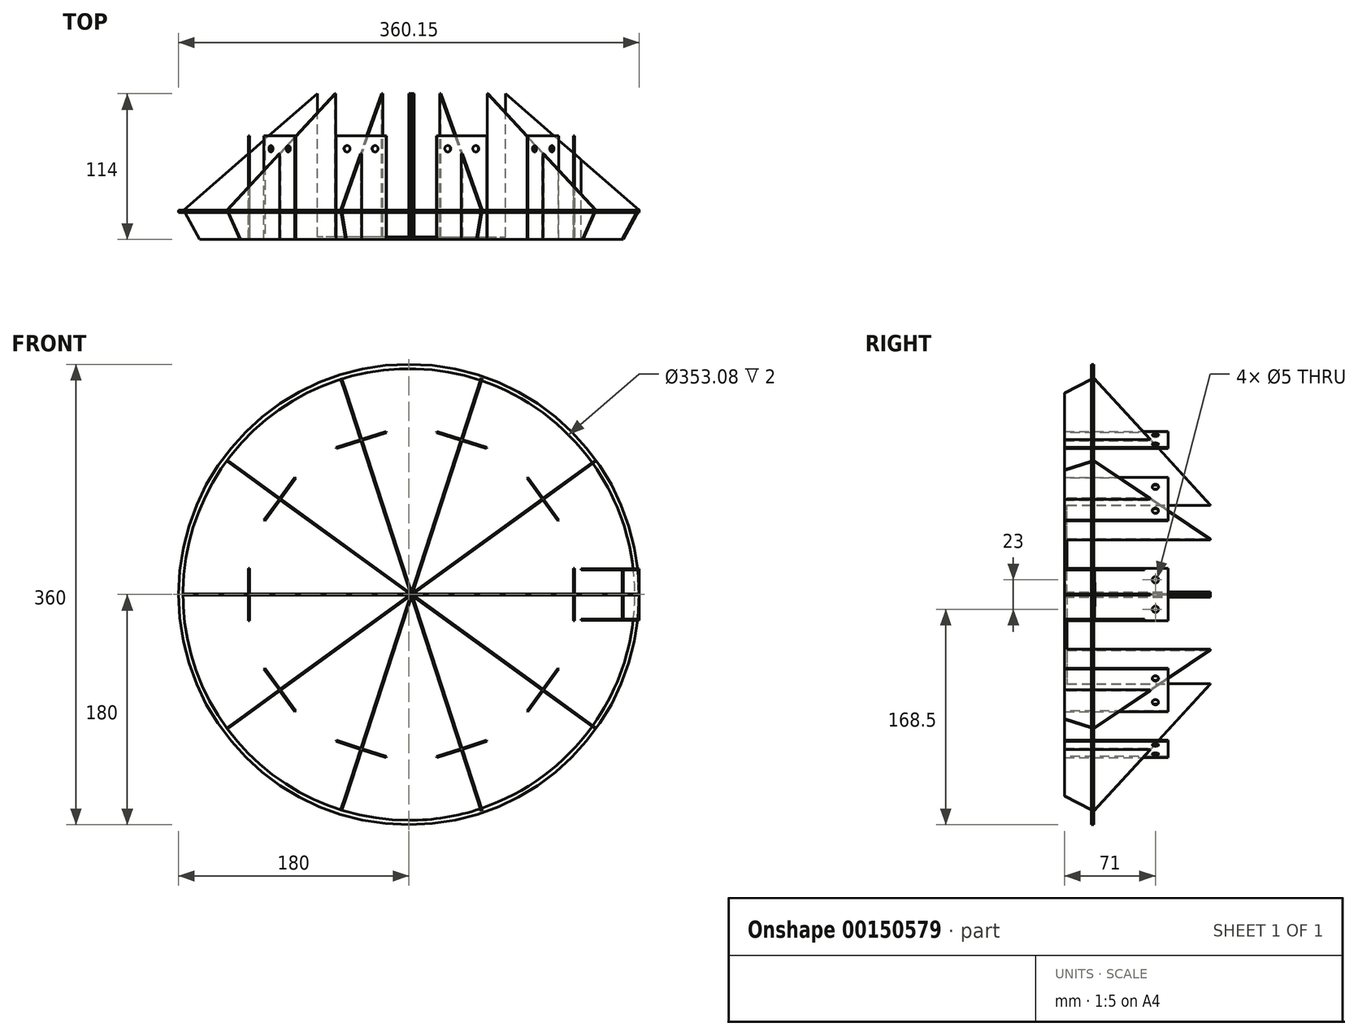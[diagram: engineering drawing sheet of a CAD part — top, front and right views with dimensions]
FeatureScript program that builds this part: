
annotation { "Feature Type Name" : "Feature", "Feature Type Description" : "" }
export const myFeature = defineFeature(function(context is Context, id is Id, definition is map)
    precondition{}
    {
        {
            var Q0;
            Q0=qCreatedBy(makeId("Top.planeOp"),FACE);
            var sketch = newSketch(context, id + "F0", { "sketchPlane" : qUnion([Q0])});
            skLineSegment(sketch, "E0", {"start": v(75.5, 0) * mm, "end": v(180, 0) * mm});
            skLineSegment(sketch, "E1", {"start": v(0, 0) * mm, "end": v(0, -23) * mm, "construction": true});
            skLineSegment(sketch, "E2", {"start": v(75.5, -23) * mm, "end": v(167.5, -23) * mm});
            skLineSegment(sketch, "E3", {"start": v(167.5, -23) * mm, "end": v(180, 0) * mm});
            skLineSegment(sketch, "E4", {"start": v(0, 91) * mm, "end": v(75.5, 91) * mm, "construction": true});
            skLineSegment(sketch, "E5", {"start": v(134.64, 39.5) * mm, "end": v(180, 0) * mm});
            skLineSegment(sketch, "E6", {"start": v(75.5, 39.5) * mm, "end": v(75.5, 0) * mm});
            skLineSegment(sketch, "E7", {"start": v(75.5, 0) * mm, "end": v(75.5, -23) * mm});
            skLineSegment(sketch, "E8", {"start": v(75.5, 0) * mm, "end": v(0, 0) * mm, "construction": true});
            skLineSegment(sketch, "E9", {"start": v(0, -23) * mm, "end": v(75.5, -23) * mm});
            skLineSegment(sketch, "E10", {"start": v(0, -23) * mm, "end": v(0, -21) * mm});
            skLineSegment(sketch, "E11", {"start": v(0, -21) * mm, "end": v(75.5, -21) * mm});
            skLineSegment(sketch, "E12", {"start": v(0, -21) * mm, "end": v(0, 91) * mm});
            skLineSegment(sketch, "E13", {"start": v(0, 91) * mm, "end": v(2, 91) * mm});
            skLineSegment(sketch, "E14", {"start": v(2, 91) * mm, "end": v(2, -21) * mm});
            skLineSegment(sketch, "E15", {"start": v(167.5, -23) * mm, "end": v(230.94, -23) * mm, "construction": true});
            skLineSegment(sketch, "E16", {"start": v(230.94, -23) * mm, "end": v(230.94, 39.5) * mm, "construction": true});
            skLineSegment(sketch, "E17", {"start": v(230.94, 39.5) * mm, "end": v(19.42, 39.5) * mm, "construction": true});
            skLineSegment(sketch, "E18", {"start": v(134.64, 39.5) * mm, "end": v(75.5, 39.5) * mm});
            skLineSegment(sketch, "E19", {"start": v(75.5, 39.5) * mm, "end": v(75.5, 91) * mm});
            skLineSegment(sketch, "E20", {"start": v(75.5, 91) * mm, "end": v(134.64, 39.5) * mm});
            skSolve(sketch);
        }
        {
            var Q0;
            Q0 = qSketchRegion(id + "F0", true);
            extrude(context, id + "F1", {"entities" : qUnion([Q0]), "endBound" : BoundingType.SYMMETRIC, "depth" : 1 * mm});
        }
        {
            var Q0;
            Q0=qCreatedBy(makeId("Top.planeOp"),FACE);
            var sketch = newSketch(context, id + "F2", { "sketchPlane" : qUnion([Q0])});
            skLineSegment(sketch, "E21.bottom", {"start": v(15, 5.01) * mm, "end": v(21.3, 5.01) * mm});
            skLineSegment(sketch, "E21.top", {"start": v(15, 0) * mm, "end": v(21.3, 0) * mm});
            skLineSegment(sketch, "E21.left", {"start": v(15, 5.01) * mm, "end": v(15, 0) * mm});
            skLineSegment(sketch, "E21.right", {"start": v(21.3, 5.01) * mm, "end": v(21.3, 0) * mm});
            skSolve(sketch);
        }
        {
            var Q0;
            Q0 = qSketchRegion(id + "F2", true);
            extrude(context, id + "F3", {"entities" : qUnion([Q0]), "operationType" : NewBodyOperationType.ADD, "endBound" : BoundingType.SYMMETRIC, "depth" : 38.5 * mm});
        }
        {
            var Q0;
            Q0=makeQuery(id+"F3.opExtrude","CAP_FACE",FACE,{"disambiguationData":[OSD([sQuery(id+"F2.wireOp",EDGE,"E21.bottom"),sQuery(id+"F2.wireOp",EDGE,"E21.top"),sQuery(id+"F2.wireOp",EDGE,"E21.left"),sQuery(id+"F2.wireOp",EDGE,"E21.right")])],"isStart":false});
            var sketch = newSketch(context, id + "F4", { "sketchPlane" : qUnion([Q0])});
            skLineSegment(sketch, "E22", {"start": v(75.5, 39.5) * mm, "end": v(75.5, -23) * mm, "construction": true});
            skLineSegment(sketch, "E23", {"start": v(134.5, 39.5) * mm, "end": v(134.64, 39.5) * mm});
            skLineSegment(sketch, "E24", {"start": v(134.64, 39.5) * mm, "end": v(180, 0) * mm});
            skLineSegment(sketch, "E25", {"start": v(180, 0) * mm, "end": v(167.5, -23) * mm});
            skLineSegment(sketch, "E26", {"start": v(167.5, -23) * mm, "end": v(134.5, -23) * mm});
            skLineSegment(sketch, "E27", {"start": v(134.5, -23) * mm, "end": v(134.5, 39.5) * mm});
            skLineSegment(sketch, "E28", {"start": v(75.5, -23) * mm, "end": v(134.5, -23) * mm, "construction": true});
            skLineSegment(sketch, "E29", {"start": v(75.5, 39.5) * mm, "end": v(134.64, 39.5) * mm, "construction": true});
            skSolve(sketch);
        }
        {
            var Q0;
            Q0 = qSketchRegion(id + "F4", true);
            extrude(context, id + "F5", {"entities" : qUnion([Q0]), "depth" : 1 * mm});
        }
        {
            var Q0;
            Q0=makeQuery(id+"F5.opExtrude","SWEPT_FACE",FACE,{"disambiguationData":[OSD([sQuery(id+"F4.wireOp",EDGE,"E25")])]});
            var sketch = newSketch(context, id + "F6", { "sketchPlane" : qUnion([Q0])});
            skLineSegment(sketch, "E30", {"start": v(59.78, 19.25) * mm, "end": v(59.78, 0) * mm});
            skLineSegment(sketch, "E31", {"start": v(59.78, 0) * mm, "end": v(86.26, 0) * mm});
            skLineSegment(sketch, "E32", {"start": v(86.26, 0) * mm, "end": v(85.95, 20.25) * mm});
            skLineSegment(sketch, "E33", {"start": v(85.95, 20.25) * mm, "end": v(59.78, 20.25) * mm});
            skLineSegment(sketch, "E34", {"start": v(59.78, 20.25) * mm, "end": v(59.78, 19.25) * mm});
            skSolve(sketch);
        }
        {
            var Q0;
            Q0 = qSketchRegion(id + "F6", true);
            extrude(context, id + "F7", {"entities" : qUnion([Q0]), "oppositeDirection" : true, "depth" : 1 * mm});
        }
        {
            var Q0;
            Q0=makeQuery(id+"F3.opExtrude","SWEPT_BODY",BODY,{"disambiguationData":[OSD([sQuery(id+"F2.wireOp",EDGE,"E21.bottom"),sQuery(id+"F2.wireOp",EDGE,"E21.top"),sQuery(id+"F2.wireOp",EDGE,"E21.left"),sQuery(id+"F2.wireOp",EDGE,"E21.right")])]});
            deleteBodies(context, id + "F8", {"entities" : qUnion([Q0])});
        }
        {
            var Q0;
            Q0=makeQuery(id+"F5.opExtrude","SWEPT_BODY",BODY,{"disambiguationData":[OSD([sQuery(id+"F4.wireOp",EDGE,"E22"),sQuery(id+"F4.wireOp",EDGE,"E23"),sQuery(id+"F4.wireOp",EDGE,"E24"),sQuery(id+"F4.wireOp",EDGE,"E25"),sQuery(id+"F4.wireOp",EDGE,"E26")])]});
            var Q1;
            Q1=makeQuery(id+"F7.opExtrude","SWEPT_BODY",BODY,{"disambiguationData":[OSD([sQuery(id+"F6.wireOp",EDGE,"E30"),sQuery(id+"F6.wireOp",EDGE,"E31"),sQuery(id+"F6.wireOp",EDGE,"E32"),sQuery(id+"F6.wireOp",EDGE,"E33"),sQuery(id+"F6.wireOp",EDGE,"E34")])]});
            var Q2;
            Q2=qCreatedBy(makeId("Top.planeOp"),FACE);
            mirror(context, id + "F9", {"entities" : qUnion([Q0, Q1]), "mirrorPlane" : qUnion([Q2])});
        }
        {
            var Q0;
            Q0=qCreatedBy(makeId("Top.planeOp"),FACE);
            var sketch = newSketch(context, id + "F10", { "sketchPlane" : qUnion([Q0])});
            skLineSegment(sketch, "E35", {"start": v(167.5, -23) * mm, "end": v(129.5, -23) * mm, "construction": true});
            skLineSegment(sketch, "E36", {"start": v(129.5, -23) * mm, "end": v(129.5, 58) * mm});
            skLineSegment(sketch, "E37", {"start": v(129.5, 58) * mm, "end": v(128.5, 58) * mm});
            skLineSegment(sketch, "E38", {"start": v(128.5, 58) * mm, "end": v(128.5, -23) * mm});
            skLineSegment(sketch, "E39", {"start": v(129.5, -23) * mm, "end": v(128.5, -23) * mm});
            skSolve(sketch);
        }
        {
            var Q0;
            Q0 = qSketchRegion(id + "F10", true);
            extrude(context, id + "F11", {"entities" : qUnion([Q0]), "operationType" : NewBodyOperationType.ADD, "endBound" : BoundingType.SYMMETRIC, "depth" : 41 * mm});
        }
        {
            var Q0;
            Q0=makeQuery(id+"F11.opExtrude","SWEPT_FACE",FACE,{"disambiguationData":[OSD([sQuery(id+"F10.wireOp",EDGE,"E36")])]});
            var sketch = newSketch(context, id + "F12", { "sketchPlane" : qUnion([Q0])});
            skLineSegment(sketch, "E40", {"start": v(0, 0) * mm, "end": v(0, -11.5) * mm, "construction": true});
            skLineSegment(sketch, "E41", {"start": v(0, -11.5) * mm, "end": v(48, -11.5) * mm, "construction": true});
            skCircle(sketch, "E42", {"center": v(48, -11.5) * mm, "radius": 2.5 * mm});
            skLineSegment(sketch, "E43.MirrorCS", {"start": v(0, 11.5) * mm, "end": v(48, 11.5) * mm, "construction": true});
            skLineSegment(sketch, "E44.MirrorCS", {"start": v(0, 0) * mm, "end": v(0, 11.5) * mm, "construction": true});
            skCircle(sketch, "E45.MirrorC", {"center": v(48, 11.5) * mm, "radius": 2.5 * mm});
            skSolve(sketch);
        }
        {
            var Q0;
            Q0 = qSketchRegion(id + "F12", true);
            extrude(context, id + "F13", {"entities" : qUnion([Q0]), "operationType" : NewBodyOperationType.REMOVE, "oppositeDirection" : true, "depth" : 25 * mm});
        }
        {
            var Q0;
            Q0=makeQuery(id+"F1.opExtrude","SWEPT_BODY",BODY,{"disambiguationData":[OSD([sQuery(id+"F0.wireOp",EDGE,"E2"),sQuery(id+"F0.wireOp",EDGE,"E3"),sQuery(id+"F0.wireOp",EDGE,"E5"),sQuery(id+"F0.wireOp",EDGE,"E6"),sQuery(id+"F0.wireOp",EDGE,"E7"),sQuery(id+"F0.wireOp",EDGE,"E9"),sQuery(id+"F0.wireOp",EDGE,"E10"),sQuery(id+"F0.wireOp",EDGE,"E11"),sQuery(id+"F0.wireOp",EDGE,"E12"),sQuery(id+"F0.wireOp",EDGE,"E13"),sQuery(id+"F0.wireOp",EDGE,"E14"),sQuery(id+"F0.wireOp",EDGE,"E19"),sQuery(id+"F0.wireOp",EDGE,"E20")])]});
            var Q1;
            Q1=sQuery(id+"F0.wireOp",EDGE,"E14");
            circularPattern(context, id + "F14", {"entities" : qUnion([Q0]), "axis" : qUnion([Q1]), "angle" : 36 * degree, "instanceCount" : 10});
        }
        {
            var Q0;
            Q0=qCreatedBy(makeId("Front.planeOp"),FACE);
            var sketch = newSketch(context, id + "F15", { "sketchPlane" : qUnion([Q0])});
            skCircle(sketch, "E46", {"center": v(0, 0) * mm, "radius": 180 * mm});
            skCircle(sketch, "E47", {"center": v(0, 0) * mm, "radius": 176.54 * mm});
            skSolve(sketch);
        }
        {
            var Q0;
            Q0 = qSketchRegion(id + "F15", true);
            extrude(context, id + "F16", {"entities" : qUnion([Q0]), "depth" : 2 * mm});
        }
    });
